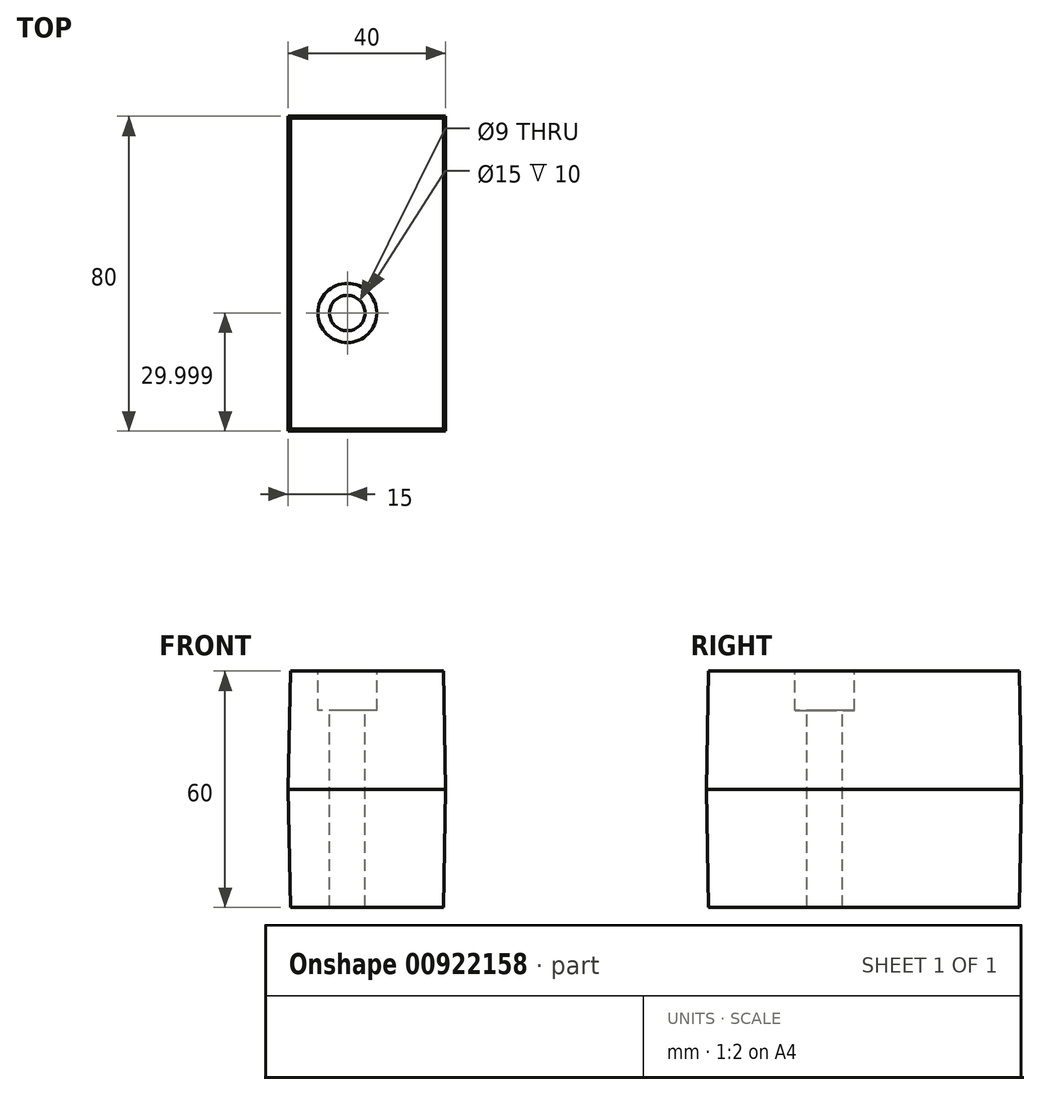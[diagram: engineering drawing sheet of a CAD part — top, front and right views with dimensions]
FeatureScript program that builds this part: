
annotation { "Feature Type Name" : "Feature", "Feature Type Description" : "" }
export const myFeature = defineFeature(function(context is Context, id is Id, definition is map)
    precondition{}
    {
        {
            var Q0;
            Q0=qCreatedBy(makeId("Top.planeOp"),FACE);
            var sketch = newSketch(context, id + "F0", { "sketchPlane" : qUnion([Q0])});
            skLineSegment(sketch, "E0", {"start": v(-20, 37.25) * mm, "end": v(-20, -42.75) * mm});
            skLineSegment(sketch, "E1", {"start": v(0, 28.98) * mm, "end": v(0, -31.53) * mm, "construction": true});
            skLineSegment(sketch, "E2.MirrorCS", {"start": v(20, 37.25) * mm, "end": v(20, -42.75) * mm});
            skLineSegment(sketch, "E3", {"start": v(-20, -42.75) * mm, "end": v(20, -42.75) * mm});
            skLineSegment(sketch, "E4", {"start": v(-20, 37.25) * mm, "end": v(20, 37.25) * mm});
            skSolve(sketch);
        }
        {
            var Q0;
            Q0=makeQuery(id+"F0.imprint","IMPRINT",FACE,{"disambiguationData":[TD([[makeQuery(id+"F0.imprint","IMPRINT",EDGE,{"derivedFrom":sQuery(id+"F0.wireOp",EDGE,"E0")}),1.0]])]});
            extrude(context, id + "F1", {"entities" : qUnion([Q0]), "endBound" : BoundingType.SYMMETRIC, "depth" : 60 * mm, "offsetDistance" : 25 * mm, "hasDraft" : true, "draftAngle" : 1 * degree, "draftPullDirection" : true});
        }
        {
            var Q0;
            Q0=makeQuery(id+"F1.opExtrude","CAP_FACE",FACE,{"disambiguationData":[OSD([sQuery(id+"F0.wireOp",EDGE,"E0"),sQuery(id+"F0.wireOp",EDGE,"E2.MirrorCS"),sQuery(id+"F0.wireOp",EDGE,"E3"),sQuery(id+"F0.wireOp",EDGE,"E4")])],"isStart":false});
            var sketch = newSketch(context, id + "F2", { "sketchPlane" : qUnion([Q0])});
            skPoint(sketch, "E5", {"position": v(-5, -12.75) * mm});
            skSolve(sketch);
        }
        {
            var Q0;
            Q0=sQuery(id+"F2.wireOp",VERTEX,"E5");
            var Q1;
            Q1=makeQuery(id+"F1.*.split.splitOp","SPLIT",BODY,{"derivedFrom":makeQuery(id+"F1.opExtrude","SWEPT_BODY",BODY,{"disambiguationData":[OSD([sQuery(id+"F0.wireOp",EDGE,"E0"),sQuery(id+"F0.wireOp",EDGE,"E2.MirrorCS"),sQuery(id+"F0.wireOp",EDGE,"E3"),sQuery(id+"F0.wireOp",EDGE,"E4")])]})});
            hole(context, id + "F3", {"style" : HoleStyle.C_BORE, "endStyle" : HoleEndStyle.THROUGH, "holeDiameter" : 9 * mm, "cBoreDiameter" : 15 * mm, "cBoreDepth" : 10 * mm, "majorDiameter" : 5 * mm, "isTappedThrough" : true, "tappedDepth" : 12 * mm, "tapClearance" : 3, "locations" : qUnion([Q0]), "scope" : qUnion([Q1])});
        }
    });
